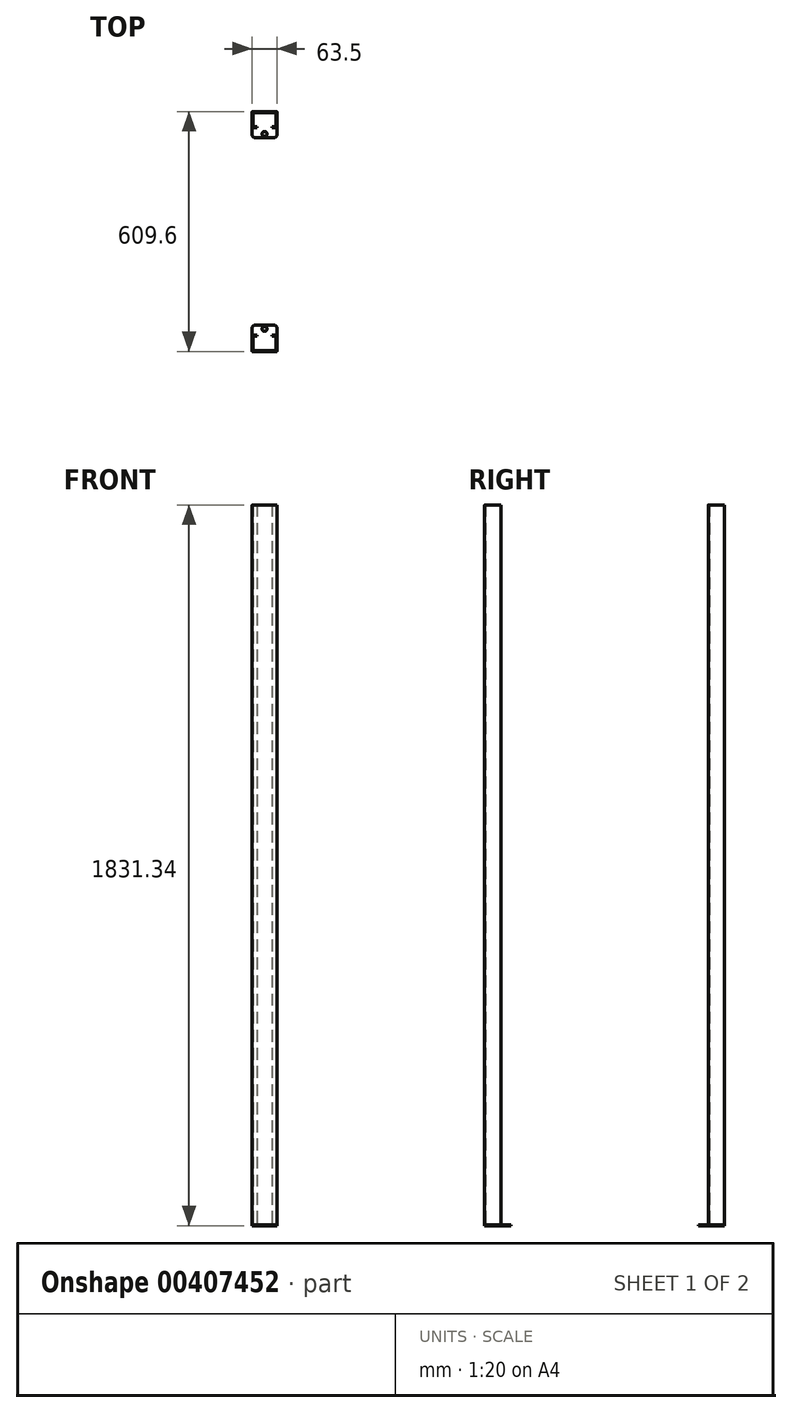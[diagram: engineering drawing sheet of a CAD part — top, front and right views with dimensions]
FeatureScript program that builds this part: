
annotation { "Feature Type Name" : "Feature", "Feature Type Description" : "" }
export const myFeature = defineFeature(function(context is Context, id is Id, definition is map)
    precondition{}
    {
        {
            var Q0;
            Q0=qCreatedBy(makeId("Top.planeOp"),FACE);
            var sketch = newSketch(context, id + "F0", { "sketchPlane" : qUnion([Q0])});
            skLineSegment(sketch, "E0.bottom", {"start": v(26.67, -238.12) * mm, "end": v(-26.67, -238.12) * mm});
            skLineSegment(sketch, "E0.top", {"start": v(31.75, -304.8) * mm, "end": v(-31.75, -304.8) * mm});
            skLineSegment(sketch, "E0.left", {"start": v(31.75, -243.2) * mm, "end": v(31.75, -304.8) * mm});
            skLineSegment(sketch, "E0.right", {"start": v(-31.75, -243.2) * mm, "end": v(-31.75, -304.8) * mm});
            skCircle(sketch, "E1", {"center": v(0, -247.65) * mm, "radius": 6.35 * mm});
            skLineSegment(sketch, "E2", {"start": v(26.67, -238.12) * mm, "end": v(31.75, -243.2) * mm});
            skLineSegment(sketch, "E3", {"start": v(-26.67, -238.13) * mm, "end": v(-31.75, -243.2) * mm});
            skLineSegment(sketch, "E4.MirrorCS", {"start": v(26.67, 238.12) * mm, "end": v(31.75, 243.2) * mm});
            skLineSegment(sketch, "E5.MirrorCS", {"start": v(-26.67, 238.13) * mm, "end": v(-31.75, 243.2) * mm});
            skCircle(sketch, "E6.MirrorC", {"center": v(0, 247.65) * mm, "radius": 6.35 * mm});
            skLineSegment(sketch, "E7.MirrorCS", {"start": v(26.67, 238.12) * mm, "end": v(-26.67, 238.12) * mm});
            skLineSegment(sketch, "E8.MirrorCS", {"start": v(31.75, 304.8) * mm, "end": v(-31.75, 304.8) * mm});
            skLineSegment(sketch, "E9.MirrorCS", {"start": v(-31.75, 243.2) * mm, "end": v(-31.75, 304.8) * mm});
            skLineSegment(sketch, "E10.MirrorCS", {"start": v(31.75, 243.2) * mm, "end": v(31.75, 304.8) * mm});
            skSolve(sketch);
        }
        {
            var Q0;
            Q0 = qSketchRegion(id + "F0", true);
            extrude(context, id + "F1", {"entities" : qUnion([Q0]), "depth" : 2.54 * mm});
        }
        {
            var Q0;
            Q0=makeQuery(id+"F1.opExtrude","CAP_FACE",FACE,{"disambiguationData":[OSD([sQuery(id+"F0.wireOp",EDGE,"E0.bottom"),sQuery(id+"F0.wireOp",EDGE,"E0.top"),sQuery(id+"F0.wireOp",EDGE,"E0.left"),sQuery(id+"F0.wireOp",EDGE,"E0.right"),sQuery(id+"F0.wireOp",EDGE,"E1"),sQuery(id+"F0.wireOp",EDGE,"E2"),sQuery(id+"F0.wireOp",EDGE,"E3")])],"isStart":false});
            var sketch = newSketch(context, id + "F2", { "sketchPlane" : qUnion([Q0])});
            skLineSegment(sketch, "E11.bottom", {"start": v(-28.5, -263.53) * mm, "end": v(-19.05, -263.53) * mm});
            skLineSegment(sketch, "E11.top", {"start": v(-28.5, -304.8) * mm, "end": v(28.5, -304.8) * mm});
            skLineSegment(sketch, "E11.left", {"start": v(-31.75, -266.78) * mm, "end": v(-31.75, -301.55) * mm});
            skLineSegment(sketch, "E11.right", {"start": v(31.75, -266.78) * mm, "end": v(31.75, -301.55) * mm});
            skLineSegment(sketch, "E12.bottom", {"start": v(-28.5, -266.06) * mm, "end": v(-19.05, -266.06) * mm});
            skLineSegment(sketch, "E12.top", {"start": v(-28.5, -302.26) * mm, "end": v(28.5, -302.26) * mm});
            skLineSegment(sketch, "E12.left", {"start": v(-29.21, -266.78) * mm, "end": v(-29.21, -301.55) * mm});
            skLineSegment(sketch, "E12.right", {"start": v(29.21, -266.78) * mm, "end": v(29.21, -301.55) * mm});
            skLineSegment(sketch, "E13", {"start": v(-19.05, -266.06) * mm, "end": v(-19.05, -263.53) * mm});
            skLineSegment(sketch, "E14", {"start": v(19.05, -263.53) * mm, "end": v(19.05, -266.06) * mm});
            skLineSegment(sketch, "E15.trimOffspring", {"start": v(19.05, -266.06) * mm, "end": v(28.5, -266.06) * mm});
            skLineSegment(sketch, "E16.trimOffspring", {"start": v(19.05, -263.53) * mm, "end": v(28.5, -263.53) * mm});
            skPoint(sketch, "E17.visualSharp", {"position": v(-31.75, -263.53) * mm});
            skArc(sketch, "E17.filletArc", {"start": v(-28.5, -263.53) * mm, "mid": v(-30.8, -264.48) * mm, "end": v(-31.75, -266.78) * mm});
            skPoint(sketch, "E18.visualSharp", {"position": v(-29.21, -266.06) * mm});
            skArc(sketch, "E18.filletArc", {"start": v(-28.5, -266.06) * mm, "mid": v(-29, -266.27) * mm, "end": v(-29.21, -266.78) * mm});
            skPoint(sketch, "E19.visualSharp", {"position": v(29.21, -266.06) * mm});
            skArc(sketch, "E19.filletArc", {"start": v(29.21, -266.78) * mm, "mid": v(29, -266.27) * mm, "end": v(28.5, -266.06) * mm});
            skPoint(sketch, "E20.visualSharp", {"position": v(31.75, -263.53) * mm});
            skArc(sketch, "E20.filletArc", {"start": v(31.75, -266.78) * mm, "mid": v(30.8, -264.48) * mm, "end": v(28.5, -263.53) * mm});
            skPoint(sketch, "E21.visualSharp", {"position": v(31.75, -304.8) * mm});
            skArc(sketch, "E21.filletArc", {"start": v(28.5, -304.8) * mm, "mid": v(30.8, -303.85) * mm, "end": v(31.75, -301.55) * mm});
            skPoint(sketch, "E22.visualSharp", {"position": v(29.21, -302.26) * mm});
            skArc(sketch, "E22.filletArc", {"start": v(28.5, -302.26) * mm, "mid": v(29, -302.05) * mm, "end": v(29.21, -301.55) * mm});
            skPoint(sketch, "E23.visualSharp", {"position": v(-29.21, -302.26) * mm});
            skArc(sketch, "E23.filletArc", {"start": v(-29.21, -301.55) * mm, "mid": v(-29, -302.05) * mm, "end": v(-28.5, -302.26) * mm});
            skPoint(sketch, "E24.visualSharp", {"position": v(-31.75, -304.8) * mm});
            skArc(sketch, "E24.filletArc", {"start": v(-31.75, -301.55) * mm, "mid": v(-30.8, -303.85) * mm, "end": v(-28.5, -304.8) * mm});
            skArc(sketch, "E25.MirrorCS", {"start": v(-28.5, 266.06) * mm, "mid": v(-29, 266.27) * mm, "end": v(-29.21, 266.78) * mm});
            skArc(sketch, "E26.MirrorCS", {"start": v(-29.21, 301.55) * mm, "mid": v(-29, 302.05) * mm, "end": v(-28.5, 302.26) * mm});
            skArc(sketch, "E27.MirrorCS", {"start": v(29.21, 266.78) * mm, "mid": v(29, 266.27) * mm, "end": v(28.5, 266.06) * mm});
            skArc(sketch, "E28.MirrorCS", {"start": v(28.5, 302.26) * mm, "mid": v(29, 302.05) * mm, "end": v(29.21, 301.55) * mm});
            skArc(sketch, "E29.MirrorCS", {"start": v(-28.5, 263.53) * mm, "mid": v(-30.8, 264.48) * mm, "end": v(-31.75, 266.78) * mm});
            skLineSegment(sketch, "E30.MirrorCS", {"start": v(19.05, 263.53) * mm, "end": v(19.05, 266.06) * mm});
            skLineSegment(sketch, "E31.MirrorCS", {"start": v(-19.05, 266.06) * mm, "end": v(-19.05, 263.53) * mm});
            skArc(sketch, "E32.MirrorCS", {"start": v(-31.75, 301.55) * mm, "mid": v(-30.8, 303.85) * mm, "end": v(-28.5, 304.8) * mm});
            skArc(sketch, "E33.MirrorCS", {"start": v(31.75, 266.78) * mm, "mid": v(30.8, 264.48) * mm, "end": v(28.5, 263.53) * mm});
            skLineSegment(sketch, "E34.MirrorCS", {"start": v(-28.5, 266.06) * mm, "end": v(-19.05, 266.06) * mm});
            skArc(sketch, "E35.MirrorCS", {"start": v(28.5, 304.8) * mm, "mid": v(30.8, 303.85) * mm, "end": v(31.75, 301.55) * mm});
            skPoint(sketch, "E36.MirrorP", {"position": v(31.75, 263.53) * mm});
            skLineSegment(sketch, "E37.MirrorCS", {"start": v(19.05, 263.53) * mm, "end": v(28.5, 263.53) * mm});
            skLineSegment(sketch, "E38.MirrorCS", {"start": v(19.05, 266.06) * mm, "end": v(28.5, 266.06) * mm});
            skLineSegment(sketch, "E39.MirrorCS", {"start": v(29.21, 266.78) * mm, "end": v(29.21, 301.55) * mm});
            skPoint(sketch, "E40.MirrorP", {"position": v(29.21, 266.06) * mm});
            skLineSegment(sketch, "E41.MirrorCS", {"start": v(-28.5, 302.26) * mm, "end": v(28.5, 302.26) * mm});
            skPoint(sketch, "E42.MirrorP", {"position": v(29.21, 302.26) * mm});
            skLineSegment(sketch, "E43.MirrorCS", {"start": v(31.75, 266.78) * mm, "end": v(31.75, 301.55) * mm});
            skLineSegment(sketch, "E44.MirrorCS", {"start": v(-29.21, 266.78) * mm, "end": v(-29.21, 301.55) * mm});
            skPoint(sketch, "E45.MirrorP", {"position": v(-29.21, 266.06) * mm});
            skPoint(sketch, "E46.MirrorP", {"position": v(-29.21, 302.26) * mm});
            skLineSegment(sketch, "E47.MirrorCS", {"start": v(-28.5, 304.8) * mm, "end": v(28.5, 304.8) * mm});
            skLineSegment(sketch, "E48.MirrorCS", {"start": v(-31.75, 266.78) * mm, "end": v(-31.75, 301.55) * mm});
            skLineSegment(sketch, "E49.MirrorCS", {"start": v(-28.5, 263.53) * mm, "end": v(-19.05, 263.53) * mm});
            skPoint(sketch, "E50.MirrorP", {"position": v(-31.75, 304.8) * mm});
            skPoint(sketch, "E51.MirrorP", {"position": v(-31.75, 263.53) * mm});
            skPoint(sketch, "E52.MirrorP", {"position": v(31.75, 304.8) * mm});
            skSolve(sketch);
        }
        {
            var Q0;
            Q0 = qSketchRegion(id + "F2", true);
            extrude(context, id + "F3", {"entities" : qUnion([Q0]), "depth" : 1828.8 * mm});
        }
    });
